FCSTD DOCUMENT  (FreeCAD 0.21R33668 +26 (Git))
Label: HMV080_2D_Dimensional_top_down
License: All rights reserved
LicenseURL: http://en.wikipedia.org/wiki/All_rights_reserved
objects: Sketcher::SketchObject×1
note: 1 computed .brp shape members not serialized (recipe doc carries the construction recipe); baked Part::Feature solids carry a one-line shape summary decoded from their .brp

FEATURE [Sketcher::SketchObject] Sketch
  FullyConstrained = true
  sketch-geometry (24):
    g0: LineSegment StartX=-2.1 StartY=0.7 StartZ=0 EndX=-2.75 EndY=0.7 EndZ=0
    g1: LineSegment StartX=-2.75 StartY=0.7 StartZ=0 EndX=-2.75 EndY=1.25 EndZ=0
    g2: LineSegment StartX=-2.75 StartY=1.25 StartZ=0 EndX=-2.1 EndY=1.25 EndZ=0
    g3: LineSegment StartX=-2.1 StartY=1.25 StartZ=0 EndX=-2.1 EndY=2.4 EndZ=0
    g4: LineSegment StartX=-2.1 StartY=2.4 StartZ=0 EndX=0 EndY=2.4 EndZ=0
    g5: LineSegment StartX=-2.1 StartY=0.7 StartZ=0 EndX=-2.1 EndY=0 EndZ=0
    g6: LineSegment StartX=0 StartY=2.4 StartZ=0 EndX=2.1 EndY=2.4 EndZ=0
    g7: LineSegment StartX=2.1 StartY=2.4 StartZ=0 EndX=2.1 EndY=1.25 EndZ=0
    g8: LineSegment StartX=2.1 StartY=1.25 StartZ=0 EndX=2.75 EndY=1.25 EndZ=0
    g9: LineSegment StartX=2.75 StartY=1.25 StartZ=0 EndX=2.75 EndY=0.7 EndZ=0
    g10: LineSegment StartX=2.75 StartY=0.7 StartZ=0 EndX=2.1 EndY=0.7 EndZ=0
    g11: LineSegment StartX=2.1 StartY=0.7 StartZ=0 EndX=2.1 EndY=0 EndZ=0
    g12: LineSegment StartX=2.1 StartY=0 StartZ=0 EndX=2.2 EndY=-0.3 EndZ=0
    g13: LineSegment StartX=-2.1 StartY=0 StartZ=0 EndX=-2.2 EndY=-0.3 EndZ=0
    g14: LineSegment StartX=-2.2 StartY=-0.3 StartZ=0 EndX=-2.2 EndY=-17.6 EndZ=0
    g15: LineSegment StartX=-2.2 StartY=-17.6 StartZ=0 EndX=2.2 EndY=-17.6 EndZ=0
    g16: LineSegment StartX=2.2 StartY=-17.6 StartZ=0 EndX=2.2 EndY=-0.3 EndZ=0
    g17: LineSegment StartX=2.1 StartY=0 StartZ=0 EndX=-2.1 EndY=0 EndZ=0
    g18: LineSegment StartX=2.2 StartY=-12.95 StartZ=0 EndX=-2.2 EndY=-12.95 EndZ=0
    g19: Circle CenterX=-1.4 CenterY=-2.04 CenterZ=0 NormalX=0 NormalY=0 NormalZ=1 AngleXU=0 Radius=0.4
    g20: LineSegment StartX=-2.2 StartY=-13.953 StartZ=0 EndX=0.95 EndY=-13.953 EndZ=0
    g21: LineSegment StartX=-2.2 StartY=-16.953 StartZ=0 EndX=0.95 EndY=-16.953 EndZ=0
    g22: Circle CenterX=-0.56 CenterY=-15.473 CenterZ=0 NormalX=0 NormalY=0 NormalZ=1 AngleXU=0 Radius=1.29
    g23: LineSegment StartX=0.95 StartY=-16.953 StartZ=0 EndX=0.95 EndY=-13.953 EndZ=0
  constraints (73):
    c: Horizontal(g0)
    c: Coincident(g1,g0)
    c: Vertical(g1)
    c: Coincident(g2,g1)
    c: Horizontal(g2)
    c: Coincident(g3,g2)
    c: Vertical(g3)
    c: Coincident(g4,g3)
    c: PointOnObject(g4,g-2)
    c: Horizontal(g4)
    c: DistanceX(g4,g4) = 2.1
    c: DistanceX(g2,g2) = 0.65
    c: DistanceY(g3,g3) = 1.15
    c: Coincident(g5,g0)
    c: PointOnObject(g5,g-1)
    c: Vertical(g5)
    c: DistanceY(g-1,g4) = 2.4
    c: DistanceY(g0,g3) = 1.7
    c: DistanceX(g2,g0) = 0
    c: Coincident(g6,g4)
    c: Horizontal(g6)
    c: Coincident(g7,g6)
    c: Vertical(g7)
    c: Coincident(g8,g7)
    c: Horizontal(g8)
    c: Coincident(g9,g8)
    c: Vertical(g9)
    c: Coincident(g10,g9)
    c: Horizontal(g10)
    c: Coincident(g11,g10)
    c: PointOnObject(g11,g-1)
    c: Vertical(g11)
    c: DistanceX(g7,g8) = 0.65
    c: DistanceX(g4,g6) = 2.1
    c: DistanceY(g7,g7) = 1.15
    c: DistanceX(g7,g10) = 0
    c: DistanceY(g9,g6) = 1.7
    c: Coincident(g12,g11)
    c: Coincident(g13,g5)
    c: DistanceX(g-1,g12) = 2.2
    c: DistanceX(g13,g-1) = 2.2
    c: Coincident(g14,g13)
    c: Vertical(g14)
    c: Coincident(g15,g14)
    c: Horizontal(g15)
    c: Coincident(g16,g15)
    c: Coincident(g16,g12)
    c: Vertical(g16)
    c: DistanceY(g15,g6) = 20
    c: DistanceY(g13,g5) = 0.3
    c: DistanceY(g12) = -0.3
    c: Coincident(g17,g11)
    c: Coincident(g17,g5)
    c: PointOnObject(g18,g16)
    c: PointOnObject(g18,g14)
    c: Horizontal(g18)
    c: DistanceY(g15,g18) = 4.65
    c: Diameter(g19) = 0.8
    c: DistanceX(g13,g19) = 0.8
    c: DistanceY(g19,g5) = 2.04
    c: PointOnObject(g20,g14)
    c: Horizontal(g20)
    c: DistanceY(g20,g19) = 11.913
    c: PointOnObject(g21,g14)
    c: Horizontal(g21)
    c: DistanceY(g21,g20) = 3
    c: Diameter(g22) = 2.58
    c: DistanceY(g22,g20) = 1.52
    c: DistanceX(g20,g22) = 1.64
    c: Coincident(g23,g21)
    c: Coincident(g23,g20)
    c: Vertical(g23)
    c: DistanceX(g21,g21) = 3.15
